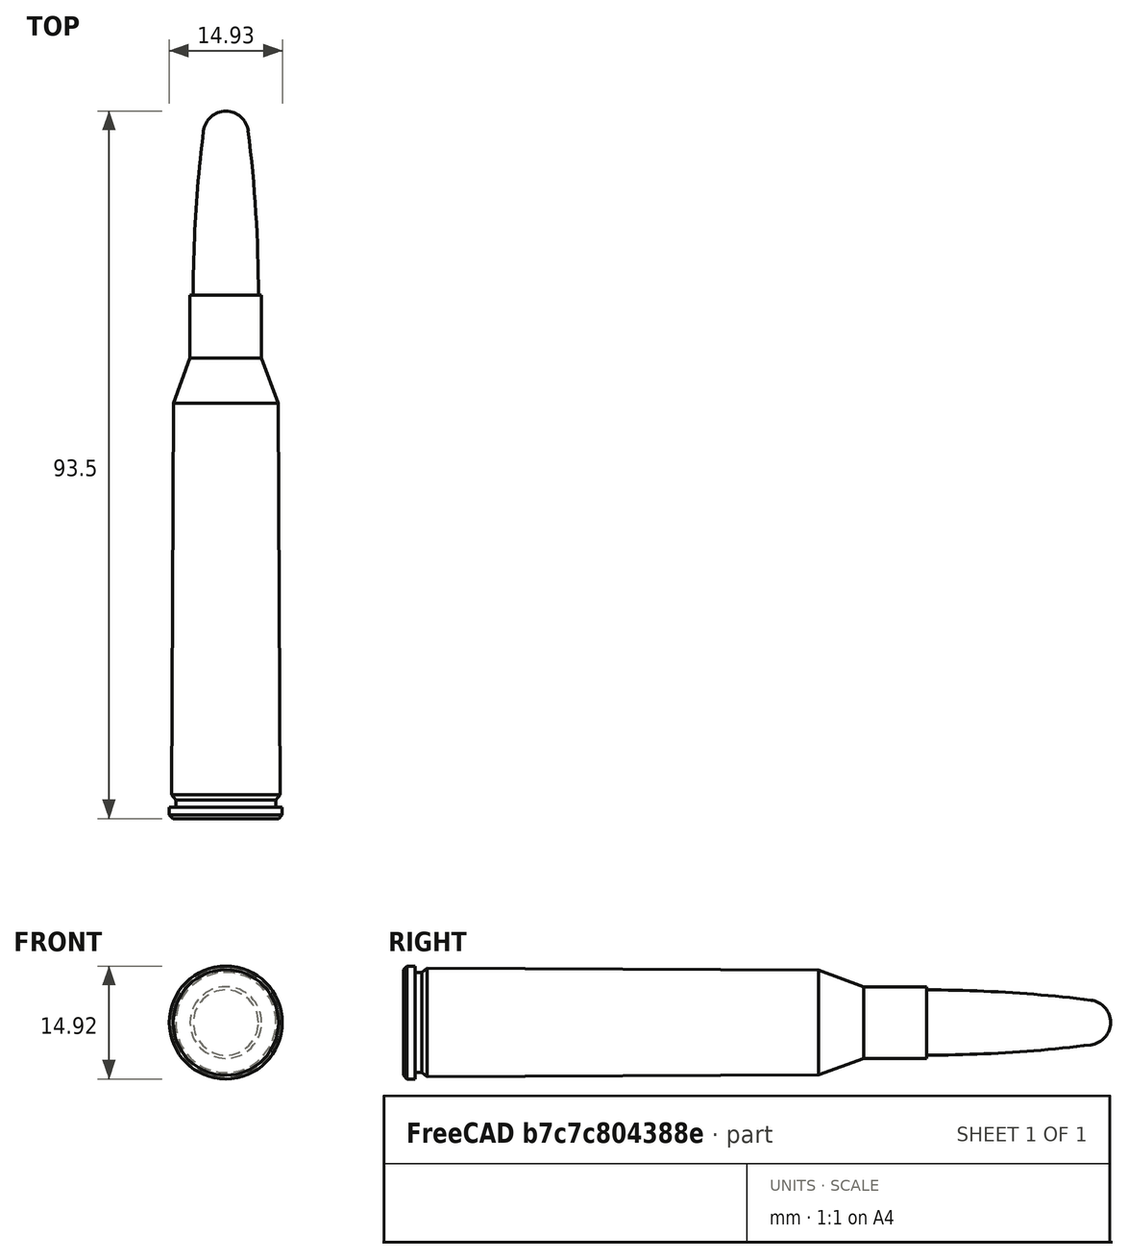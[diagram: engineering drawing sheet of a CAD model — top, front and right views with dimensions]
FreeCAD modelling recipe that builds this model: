
FCSTD DOCUMENT
Label: 338lapua
objects: Sketcher::SketchObject×1, PartDesign::Revolution×1
note: 2 computed .brp shape members not serialized (recipe doc carries the construction recipe); baked Part::Feature solids carry a one-line shape summary decoded from their .brp

FEATURE [Sketcher::SketchObject] Sketch
  sketch-geometry (18):
    g0: LineSegment StartX=0 StartY=0 StartZ=0 EndX=6.965 EndY=0 EndZ=0
    g1: LineSegment StartX=6.965 StartY=0 StartZ=0 EndX=7.465 EndY=0.5 EndZ=0
    g2: LineSegment StartX=7.465 StartY=0.5 StartZ=0 EndX=7.465 EndY=1.52 EndZ=0
    g3: LineSegment StartX=7.465 StartY=1.52 StartZ=0 EndX=6.62 EndY=1.52 EndZ=0
    g4: LineSegment StartX=6.62 StartY=1.52 StartZ=0 EndX=6.62 EndY=2.42 EndZ=0
    g5: LineSegment StartX=7.19091 StartY=3.12 StartZ=0 EndX=6.91 EndY=54.9 EndZ=0
    g6: LineSegment StartX=6.91 StartY=54.9 StartZ=0 EndX=4.73 EndY=60.89 EndZ=0
    g7: LineSegment StartX=4.73 StartY=60.89 StartZ=0 EndX=4.73 EndY=69.2 EndZ=0
    g8: LineSegment StartX=0 StartY=69.2 StartZ=0 EndX=0 EndY=0 EndZ=0
    g9: LineSegment StartX=6.62 StartY=2.42 StartZ=0 EndX=7.19091 EndY=3.12 EndZ=0
    g10: ArcOfCircle CenterX=-170.614 CenterY=69.2 CenterZ=0 NormalX=0 NormalY=0 NormalZ=1 Radius=174.919 StartAngle=8.379e-09 EndAngle=0.124329
    g11: LineSegment [constr] StartX=1.30311 StartY=104.108 StartZ=0 EndX=5.76831 EndY=68.3788 EndZ=0
    g12: LineSegment [constr] StartX=-4.37663 StartY=93.5 StartZ=0 EndX=4.04174 EndY=93.5 EndZ=0
    g13: LineSegment [constr] StartX=4.305 StartY=56.801 StartZ=0 EndX=4.305 EndY=78.022 EndZ=0
    g14: LineSegment StartX=0 StartY=93.5 StartZ=0 EndX=0 EndY=69.2 EndZ=0
    g15: ArcOfCircle CenterX=3.3526e-08 CenterY=90.5222 CenterZ=0 NormalX=0 NormalY=0 NormalZ=1 Radius=2.97781 StartAngle=0.124329 EndAngle=1.5708
    g16: LineSegment StartX=4.305 StartY=69.2 StartZ=0 EndX=4.73 EndY=69.2 EndZ=0
    g17: LineSegment [constr] StartX=0 StartY=69.2 StartZ=0 EndX=4.305 EndY=69.2 EndZ=0
  constraints (54):
    c: Horizontal(g0)
    c: Coincident(g0,g1)
    c: Coincident(g1,g2)
    c: Vertical(g2)
    c: Coincident(g2,g3)
    c: Horizontal(g3)
    c: Coincident(g3,g4)
    c: Coincident(g5,g6)
    c: Coincident(g6,g7)
    c: Vertical(g7)
    c: Coincident(g8,g0)
    c: Vertical(g8)
    c: Coincident(g9,g4)
    c: Coincident(g9,g5)
    c: Vertical(g4)
    c: DistanceY(g0) = 0
    c: DistanceY(g1) = 0.5
    c: Angle(g1) = 0.785398
    c: DistanceY(g2) = 1.52
    c: DistanceY(g4) = 0.9
    c: DistanceY(g5) = 3.12
    c: DistanceY(g5) = 54.9
    c: Angle(g9) = 0.886627
    c: DistanceY(g6) = 60.89
    c: DistanceY(g7) = 69.2
    c: DistanceX(g0) = 0
    c: DistanceX(g1) = 7.465
    c: DistanceX(g3) = 6.62
    c: DistanceX(g5) = 6.91
    c: DistanceX(g6) = 4.73
    c: Tangent(g10,g11)
    c: Horizontal(g12)
    c: Vertical(g13)
    c: PointOnObject(g10,g13)
    c: Tangent(g13,g10)
    c: PointOnObject(g10,g11)
    c: Vertical(g14)
    c: DistanceX(g10) = 4.305
    c: Coincident(g15,g14)
    c: Coincident(g15,g10)
    c: Tangent(g15,g11)
    c: Tangent(g15,g12)
    c: PointOnObject(g14,g12)
    c: DistanceY(g14) = 93.5
    c: Distance(g11) = 36.007
    c: Distance(g12) = 8.41837
    c: Distance(g13) = 21.221
    c: Coincident(g16,g10)
    c: Coincident(g16,g7)
    c: Horizontal(g16)
    c: Coincident(g14,g8)
    c: Coincident(g17,g8)
    c: Coincident(g17,g10)
    c: Horizontal(g17)
FEATURE [PartDesign::Revolution] Revolution
  Angle = 360
  Axis = (0,1,0)
  Base = (0,0,0)
  Sketch = -> Sketch
